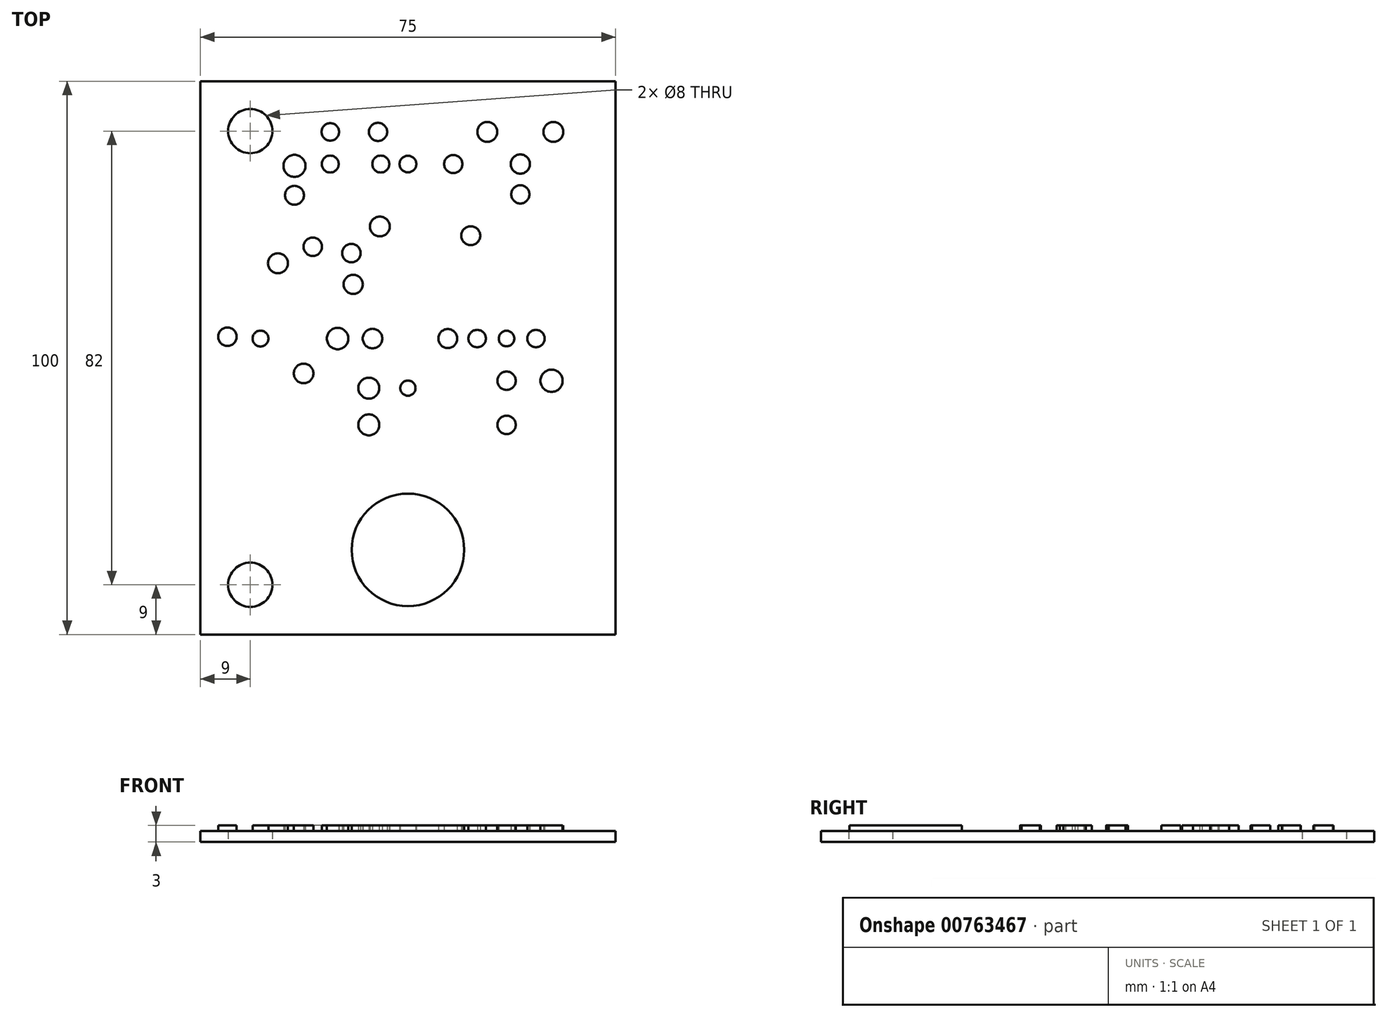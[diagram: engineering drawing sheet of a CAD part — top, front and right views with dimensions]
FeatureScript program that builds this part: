
annotation { "Feature Type Name" : "Feature", "Feature Type Description" : "" }
export const myFeature = defineFeature(function(context is Context, id is Id, definition is map)
    precondition{}
    {
        {
            var Q0;
            Q0=qCreatedBy(makeId("Top.planeOp"),FACE);
            var sketch = newSketch(context, id + "F0", { "sketchPlane" : qUnion([Q0])});
            skLineSegment(sketch, "E0.bottom", {"start": v(-37.5, 50) * mm, "end": v(37.5, 50) * mm});
            skLineSegment(sketch, "E0.top", {"start": v(-37.5, -50) * mm, "end": v(37.5, -50) * mm});
            skLineSegment(sketch, "E0.left", {"start": v(-37.5, 50) * mm, "end": v(-37.5, -50) * mm});
            skLineSegment(sketch, "E0.right", {"start": v(37.5, 50) * mm, "end": v(37.5, -50) * mm});
            skPoint(sketch, "E0.middle", {"position": v(0, 0) * mm});
            skCircle(sketch, "E1", {"center": v(-28.5, 41) * mm, "radius": 4 * mm});
            skCircle(sketch, "E2", {"center": v(-28.5, -41) * mm, "radius": 4 * mm});
            skSolve(sketch);
        }
        {
            var Q0;
            Q0=makeQuery(id+"F0.imprint","IMPRINT",FACE,{"disambiguationData":[TD([[makeQuery(id+"F0.imprint","IMPRINT",EDGE,{"derivedFrom":sQuery(id+"F0.wireOp",EDGE,"E0.bottom")}),-1.0]])]});
            extrude(context, id + "F1", {"entities" : qUnion([Q0]), "depth" : 2 * mm, "offsetDistance" : 25 * mm});
        }
        {
            var Q0;
            Q0=makeQuery(id+"F1.opExtrude","CAP_FACE",FACE,{"disambiguationData":[OSD([sQuery(id+"F0.wireOp",EDGE,"E0.bottom"),sQuery(id+"F0.wireOp",EDGE,"E0.top"),sQuery(id+"F0.wireOp",EDGE,"E0.left"),sQuery(id+"F0.wireOp",EDGE,"E0.right"),sQuery(id+"F0.wireOp",EDGE,"E1"),sQuery(id+"F0.wireOp",EDGE,"E2")])],"isStart":false});
            var sketch = newSketch(context, id + "F2", { "sketchPlane" : qUnion([Q0])});
            skCircle(sketch, "E3", {"center": v(-20.52, 29.4) * mm, "radius": 1.7 * mm});
            skCircle(sketch, "E4", {"center": v(-20.52, 34.71) * mm, "radius": 2 * mm});
            skCircle(sketch, "E5", {"center": v(-14.04, 35.05) * mm, "radius": 1.53 * mm});
            skCircle(sketch, "E6", {"center": v(-14.04, 40.85) * mm, "radius": 1.57 * mm});
            skCircle(sketch, "E7", {"center": v(-4.91, 35.05) * mm, "radius": 1.53 * mm});
            skCircle(sketch, "E8", {"center": v(0, 35.05) * mm, "radius": 1.5 * mm});
            skCircle(sketch, "E9", {"center": v(-5.41, 40.85) * mm, "radius": 1.64 * mm});
            skCircle(sketch, "E10", {"center": v(8.2, 35.05) * mm, "radius": 1.64 * mm});
            skCircle(sketch, "E11", {"center": v(14.34, 40.85) * mm, "radius": 1.8 * mm});
            skCircle(sketch, "E12", {"center": v(20.32, 29.57) * mm, "radius": 1.64 * mm});
            skCircle(sketch, "E13", {"center": v(20.32, 35.05) * mm, "radius": 1.73 * mm});
            skCircle(sketch, "E14", {"center": v(26.3, 40.85) * mm, "radius": 1.8 * mm});
            skCircle(sketch, "E15", {"center": v(-23.5, 17.12) * mm, "radius": 1.8 * mm});
            skCircle(sketch, "E16", {"center": v(-17.2, 20.1) * mm, "radius": 1.67 * mm});
            skCircle(sketch, "E17", {"center": v(-9.9, 13.3) * mm, "radius": 1.73 * mm});
            skCircle(sketch, "E18", {"center": v(-10.23, 18.94) * mm, "radius": 1.66 * mm});
            skCircle(sketch, "E19", {"center": v(-5.08, 23.76) * mm, "radius": 1.79 * mm});
            skCircle(sketch, "E20", {"center": v(11.35, 22.1) * mm, "radius": 1.7 * mm});
            skCircle(sketch, "E21", {"center": v(-32.63, 3.84) * mm, "radius": 1.66 * mm});
            skCircle(sketch, "E22", {"center": v(-26.66, 3.5) * mm, "radius": 1.43 * mm});
            skCircle(sketch, "E23", {"center": v(-18.86, -2.8) * mm, "radius": 1.76 * mm});
            skCircle(sketch, "E24", {"center": v(-12.72, 3.5) * mm, "radius": 1.94 * mm});
            skCircle(sketch, "E25", {"center": v(-7.07, -5.46) * mm, "radius": 1.9 * mm});
            skCircle(sketch, "E26", {"center": v(-6.4, 3.5) * mm, "radius": 1.76 * mm});
            skCircle(sketch, "E27", {"center": v(-7.07, -12.1) * mm, "radius": 1.9 * mm});
            skCircle(sketch, "E28", {"center": v(0, -5.46) * mm, "radius": 1.37 * mm});
            skCircle(sketch, "E29", {"center": v(7.2, 3.5) * mm, "radius": 1.7 * mm});
            skCircle(sketch, "E30", {"center": v(12.52, 3.5) * mm, "radius": 1.57 * mm});
            skCircle(sketch, "E31", {"center": v(17.83, 3.5) * mm, "radius": 1.4 * mm});
            skCircle(sketch, "E32", {"center": v(17.83, -4.13) * mm, "radius": 1.66 * mm});
            skCircle(sketch, "E33", {"center": v(17.83, -12.1) * mm, "radius": 1.66 * mm});
            skCircle(sketch, "E34", {"center": v(25.96, -4.13) * mm, "radius": 2 * mm});
            skCircle(sketch, "E35", {"center": v(23.14, 3.5) * mm, "radius": 1.57 * mm});
            skSolve(sketch);
        }
        {
            var Q0;
            Q0=makeQuery(id+"F2.imprint","IMPRINT",FACE,{"disambiguationData":[TD([[makeQuery(id+"F2.imprint","IMPRINT",EDGE,{"derivedFrom":sQuery(id+"F2.wireOp",EDGE,"E3")}),-1.0]])]});
            var sketch = newSketch(context, id + "F3", { "sketchPlane" : qUnion([Q0])});
            skCircle(sketch, "E36", {"center": v(0, -34.69) * mm, "radius": 10.17 * mm});
            skSolve(sketch);
        }
        {
            var Q0;
            Q0=makeQuery(id+"F3.imprint","IMPRINT",FACE,{"disambiguationData":[TD([[makeQuery(id+"F3.imprint","IMPRINT",EDGE,{"derivedFrom":sQuery(id+"F3.wireOp",EDGE,"E36")}),1.0]])]});
            var Q1;
            Q1=makeQuery(id+"F2.imprint","IMPRINT",FACE,{"disambiguationData":[TD([[makeQuery(id+"F2.imprint","IMPRINT",EDGE,{"derivedFrom":sQuery(id+"F2.wireOp",EDGE,"E28")}),1.0]])]});
            var Q2;
            Q2=makeQuery(id+"F2.imprint","IMPRINT",FACE,{"disambiguationData":[TD([[makeQuery(id+"F2.imprint","IMPRINT",EDGE,{"derivedFrom":sQuery(id+"F2.wireOp",EDGE,"E25")}),1.0]])]});
            var Q3;
            Q3=makeQuery(id+"F2.imprint","IMPRINT",FACE,{"disambiguationData":[TD([[makeQuery(id+"F2.imprint","IMPRINT",EDGE,{"derivedFrom":sQuery(id+"F2.wireOp",EDGE,"E27")}),1.0]])]});
            var Q4;
            Q4=makeQuery(id+"F2.imprint","IMPRINT",FACE,{"disambiguationData":[TD([[makeQuery(id+"F2.imprint","IMPRINT",EDGE,{"derivedFrom":sQuery(id+"F2.wireOp",EDGE,"E33")}),1.0]])]});
            var Q5;
            Q5=makeQuery(id+"F2.imprint","IMPRINT",FACE,{"disambiguationData":[TD([[makeQuery(id+"F2.imprint","IMPRINT",EDGE,{"derivedFrom":sQuery(id+"F2.wireOp",EDGE,"E32")}),1.0]])]});
            var Q6;
            Q6=makeQuery(id+"F2.imprint","IMPRINT",FACE,{"disambiguationData":[TD([[makeQuery(id+"F2.imprint","IMPRINT",EDGE,{"derivedFrom":sQuery(id+"F2.wireOp",EDGE,"E34")}),1.0]])]});
            var Q7;
            Q7=makeQuery(id+"F2.imprint","IMPRINT",FACE,{"disambiguationData":[TD([[makeQuery(id+"F2.imprint","IMPRINT",EDGE,{"derivedFrom":sQuery(id+"F2.wireOp",EDGE,"E35")}),1.0]])]});
            var Q8;
            Q8=makeQuery(id+"F2.imprint","IMPRINT",FACE,{"disambiguationData":[TD([[makeQuery(id+"F2.imprint","IMPRINT",EDGE,{"derivedFrom":sQuery(id+"F2.wireOp",EDGE,"E31")}),1.0]])]});
            var Q9;
            Q9=makeQuery(id+"F2.imprint","IMPRINT",FACE,{"disambiguationData":[TD([[makeQuery(id+"F2.imprint","IMPRINT",EDGE,{"derivedFrom":sQuery(id+"F2.wireOp",EDGE,"E30")}),1.0]])]});
            var Q10;
            Q10=makeQuery(id+"F2.imprint","IMPRINT",FACE,{"disambiguationData":[TD([[makeQuery(id+"F2.imprint","IMPRINT",EDGE,{"derivedFrom":sQuery(id+"F2.wireOp",EDGE,"E29")}),1.0]])]});
            var Q11;
            Q11=makeQuery(id+"F2.imprint","IMPRINT",FACE,{"disambiguationData":[TD([[makeQuery(id+"F2.imprint","IMPRINT",EDGE,{"derivedFrom":sQuery(id+"F2.wireOp",EDGE,"E26")}),1.0]])]});
            var Q12;
            Q12=makeQuery(id+"F2.imprint","IMPRINT",FACE,{"disambiguationData":[TD([[makeQuery(id+"F2.imprint","IMPRINT",EDGE,{"derivedFrom":sQuery(id+"F2.wireOp",EDGE,"E24")}),1.0]])]});
            var Q13;
            Q13=makeQuery(id+"F2.imprint","IMPRINT",FACE,{"disambiguationData":[TD([[makeQuery(id+"F2.imprint","IMPRINT",EDGE,{"derivedFrom":sQuery(id+"F2.wireOp",EDGE,"E23")}),1.0]])]});
            var Q14;
            Q14=makeQuery(id+"F2.imprint","IMPRINT",FACE,{"disambiguationData":[TD([[makeQuery(id+"F2.imprint","IMPRINT",EDGE,{"derivedFrom":sQuery(id+"F2.wireOp",EDGE,"E22")}),1.0]])]});
            var Q15;
            Q15=makeQuery(id+"F2.imprint","IMPRINT",FACE,{"disambiguationData":[TD([[makeQuery(id+"F2.imprint","IMPRINT",EDGE,{"derivedFrom":sQuery(id+"F2.wireOp",EDGE,"E21")}),1.0]])]});
            var Q16;
            Q16=makeQuery(id+"F2.imprint","IMPRINT",FACE,{"disambiguationData":[TD([[makeQuery(id+"F2.imprint","IMPRINT",EDGE,{"derivedFrom":sQuery(id+"F2.wireOp",EDGE,"E17")}),1.0]])]});
            var Q17;
            Q17=makeQuery(id+"F2.imprint","IMPRINT",FACE,{"disambiguationData":[TD([[makeQuery(id+"F2.imprint","IMPRINT",EDGE,{"derivedFrom":sQuery(id+"F2.wireOp",EDGE,"E18")}),1.0]])]});
            var Q18;
            Q18=makeQuery(id+"F2.imprint","IMPRINT",FACE,{"disambiguationData":[TD([[makeQuery(id+"F2.imprint","IMPRINT",EDGE,{"derivedFrom":sQuery(id+"F2.wireOp",EDGE,"E16")}),1.0]])]});
            var Q19;
            Q19=makeQuery(id+"F2.imprint","IMPRINT",FACE,{"disambiguationData":[TD([[makeQuery(id+"F2.imprint","IMPRINT",EDGE,{"derivedFrom":sQuery(id+"F2.wireOp",EDGE,"E15")}),1.0]])]});
            var Q20;
            Q20=makeQuery(id+"F2.imprint","IMPRINT",FACE,{"disambiguationData":[TD([[makeQuery(id+"F2.imprint","IMPRINT",EDGE,{"derivedFrom":sQuery(id+"F2.wireOp",EDGE,"E19")}),1.0]])]});
            var Q21;
            Q21=makeQuery(id+"F2.imprint","IMPRINT",FACE,{"disambiguationData":[TD([[makeQuery(id+"F2.imprint","IMPRINT",EDGE,{"derivedFrom":sQuery(id+"F2.wireOp",EDGE,"E20")}),1.0]])]});
            var Q22;
            Q22=makeQuery(id+"F2.imprint","IMPRINT",FACE,{"disambiguationData":[TD([[makeQuery(id+"F2.imprint","IMPRINT",EDGE,{"derivedFrom":sQuery(id+"F2.wireOp",EDGE,"E12")}),1.0]])]});
            var Q23;
            Q23=makeQuery(id+"F2.imprint","IMPRINT",FACE,{"disambiguationData":[TD([[makeQuery(id+"F2.imprint","IMPRINT",EDGE,{"derivedFrom":sQuery(id+"F2.wireOp",EDGE,"E13")}),1.0]])]});
            var Q24;
            Q24=makeQuery(id+"F2.imprint","IMPRINT",FACE,{"disambiguationData":[TD([[makeQuery(id+"F2.imprint","IMPRINT",EDGE,{"derivedFrom":sQuery(id+"F2.wireOp",EDGE,"E14")}),1.0]])]});
            var Q25;
            Q25=makeQuery(id+"F2.imprint","IMPRINT",FACE,{"disambiguationData":[TD([[makeQuery(id+"F2.imprint","IMPRINT",EDGE,{"derivedFrom":sQuery(id+"F2.wireOp",EDGE,"E11")}),1.0]])]});
            var Q26;
            Q26=makeQuery(id+"F2.imprint","IMPRINT",FACE,{"disambiguationData":[TD([[makeQuery(id+"F2.imprint","IMPRINT",EDGE,{"derivedFrom":sQuery(id+"F2.wireOp",EDGE,"E10")}),1.0]])]});
            var Q27;
            Q27=makeQuery(id+"F2.imprint","IMPRINT",FACE,{"disambiguationData":[TD([[makeQuery(id+"F2.imprint","IMPRINT",EDGE,{"derivedFrom":sQuery(id+"F2.wireOp",EDGE,"E8")}),1.0]])]});
            var Q28;
            Q28=makeQuery(id+"F2.imprint","IMPRINT",FACE,{"disambiguationData":[TD([[makeQuery(id+"F2.imprint","IMPRINT",EDGE,{"derivedFrom":sQuery(id+"F2.wireOp",EDGE,"E7")}),1.0]])]});
            var Q29;
            Q29=makeQuery(id+"F2.imprint","IMPRINT",FACE,{"disambiguationData":[TD([[makeQuery(id+"F2.imprint","IMPRINT",EDGE,{"derivedFrom":sQuery(id+"F2.wireOp",EDGE,"E9")}),1.0]])]});
            var Q30;
            Q30=makeQuery(id+"F2.imprint","IMPRINT",FACE,{"disambiguationData":[TD([[makeQuery(id+"F2.imprint","IMPRINT",EDGE,{"derivedFrom":sQuery(id+"F2.wireOp",EDGE,"E6")}),1.0]])]});
            var Q31;
            Q31=makeQuery(id+"F2.imprint","IMPRINT",FACE,{"disambiguationData":[TD([[makeQuery(id+"F2.imprint","IMPRINT",EDGE,{"derivedFrom":sQuery(id+"F2.wireOp",EDGE,"E5")}),1.0]])]});
            var Q32;
            Q32=makeQuery(id+"F2.imprint","IMPRINT",FACE,{"disambiguationData":[TD([[makeQuery(id+"F2.imprint","IMPRINT",EDGE,{"derivedFrom":sQuery(id+"F2.wireOp",EDGE,"E4")}),1.0]])]});
            var Q33;
            Q33=makeQuery(id+"F2.imprint","IMPRINT",FACE,{"disambiguationData":[TD([[makeQuery(id+"F2.imprint","IMPRINT",EDGE,{"derivedFrom":sQuery(id+"F2.wireOp",EDGE,"E3")}),1.0]])]});
            extrude(context, id + "F4", {"entities" : qUnion([Q0, Q1, Q2, Q3, Q4, Q5, Q6, Q7, Q8, Q9, Q10, Q11, Q12, Q13, Q14, Q15, Q16, Q17, Q18, Q19, Q20, Q21, Q22, Q23, Q24, Q25, Q26, Q27, Q28, Q29, Q30, Q31, Q32, Q33]), "operationType" : NewBodyOperationType.ADD, "depth" : 1 * mm, "offsetDistance" : 25 * mm});
        }
    });
